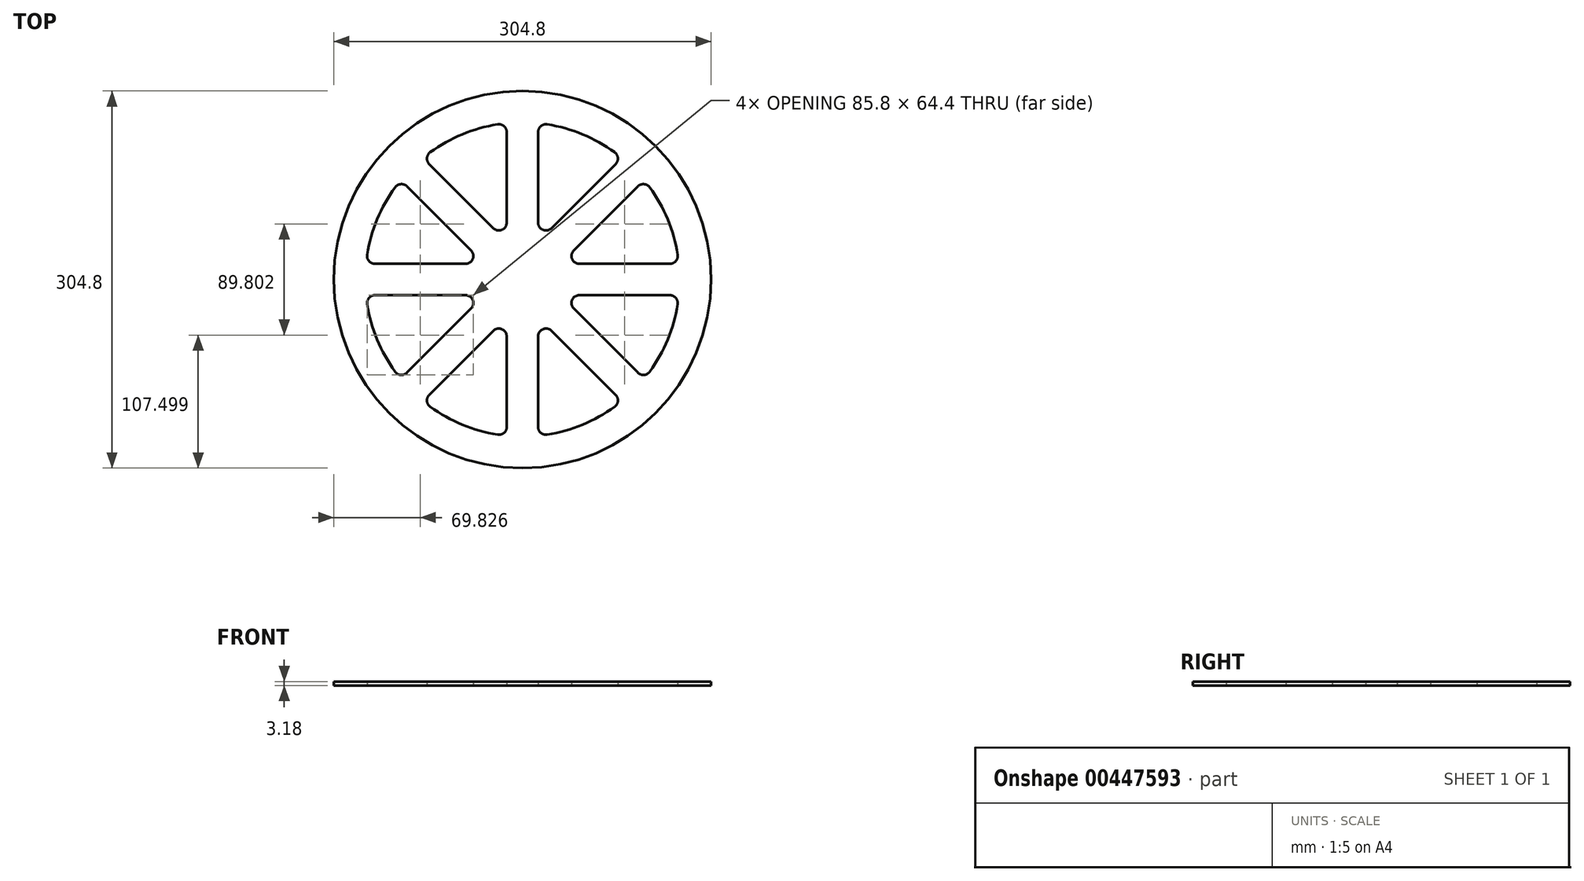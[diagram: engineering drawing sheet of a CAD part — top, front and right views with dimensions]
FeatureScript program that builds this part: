
annotation { "Feature Type Name" : "Feature", "Feature Type Description" : "" }
export const myFeature = defineFeature(function(context is Context, id is Id, definition is map)
    precondition{}
    {
        {
            var Q0;
            Q0=qCreatedBy(makeId("Top.planeOp"),FACE);
            var sketch = newSketch(context, id + "F0", { "sketchPlane" : qUnion([Q0])});
            skCircle(sketch, "E0", {"center": v(0, 0) * mm, "radius": 152.4 * mm});
            skArc(sketch, "E1", {"start": v(-125.4, -20.05) * mm, "mid": v(-117.33, -48.6) * mm, "end": v(-102.86, -74.5) * mm});
            skLineSegment(sketch, "E2.bottom", {"start": v(-119.14, 12.7) * mm, "end": v(-46, 12.7) * mm});
            skArc(sketch, "E3.trimOffspring", {"start": v(125.4, 20.05) * mm, "mid": v(117.33, 48.6) * mm, "end": v(102.86, 74.5) * mm});
            skPoint(sketch, "E4.visualSharp", {"position": v(-126.36, 12.7) * mm});
            skArc(sketch, "E4.filletArc", {"start": v(-125.4, 20.05) * mm, "mid": v(-123.97, 14.93) * mm, "end": v(-119.14, 12.7) * mm});
            skPoint(sketch, "E5.visualSharp", {"position": v(-126.36, -12.7) * mm});
            skArc(sketch, "E5.filletArc", {"start": v(-119.14, -12.7) * mm, "mid": v(-123.97, -14.93) * mm, "end": v(-125.4, -20.05) * mm});
            skPoint(sketch, "E6.visualSharp", {"position": v(126.36, -12.7) * mm});
            skArc(sketch, "E6.filletArc", {"start": v(125.4, -20.05) * mm, "mid": v(123.97, -14.93) * mm, "end": v(119.14, -12.7) * mm});
            skPoint(sketch, "E7.visualSharp", {"position": v(126.36, 12.7) * mm});
            skArc(sketch, "E7.filletArc", {"start": v(119.14, 12.7) * mm, "mid": v(123.97, 14.93) * mm, "end": v(125.4, 20.05) * mm});
            skPoint(sketch, "E8.1.0", {"position": v(80.37, 98.33) * mm});
            skPoint(sketch, "E8.1.1", {"position": v(-98.33, -80.37) * mm});
            skLineSegment(sketch, "E8.1.3", {"start": v(-93.22, -75.26) * mm, "end": v(-41.5, -23.54) * mm});
            skPoint(sketch, "E8.1.4", {"position": v(-80.37, -98.33) * mm});
            skPoint(sketch, "E8.1.5", {"position": v(98.33, 80.37) * mm});
            skLineSegment(sketch, "E8.1.6", {"start": v(-75.26, -93.22) * mm, "end": v(-23.54, -41.5) * mm});
            skArc(sketch, "E8.1.7", {"start": v(75.26, 93.22) * mm, "mid": v(77.1, 98.22) * mm, "end": v(74.5, 102.86) * mm});
            skArc(sketch, "E8.1.8", {"start": v(-75.26, -93.22) * mm, "mid": v(-77.1, -98.22) * mm, "end": v(-74.5, -102.86) * mm});
            skArc(sketch, "E8.1.9", {"start": v(-102.86, -74.5) * mm, "mid": v(-98.22, -77.1) * mm, "end": v(-93.22, -75.26) * mm});
            skArc(sketch, "E8.1.10", {"start": v(102.86, 74.5) * mm, "mid": v(98.22, 77.1) * mm, "end": v(93.22, 75.26) * mm});
            skPoint(sketch, "E8.2.0", {"position": v(-12.7, 126.36) * mm});
            skPoint(sketch, "E8.2.1", {"position": v(-12.7, -126.36) * mm});
            skLineSegment(sketch, "E8.2.3", {"start": v(-12.7, -119.14) * mm, "end": v(-12.7, -46) * mm});
            skPoint(sketch, "E8.2.4", {"position": v(12.7, -126.36) * mm});
            skPoint(sketch, "E8.2.5", {"position": v(12.7, 126.36) * mm});
            skLineSegment(sketch, "E8.2.6", {"start": v(12.7, -119.14) * mm, "end": v(12.7, -46) * mm});
            skArc(sketch, "E8.2.7", {"start": v(-12.7, 119.14) * mm, "mid": v(-14.93, 123.97) * mm, "end": v(-20.05, 125.4) * mm});
            skArc(sketch, "E8.2.8", {"start": v(12.7, -119.14) * mm, "mid": v(14.93, -123.97) * mm, "end": v(20.05, -125.4) * mm});
            skArc(sketch, "E8.2.9", {"start": v(-20.05, -125.4) * mm, "mid": v(-14.93, -123.97) * mm, "end": v(-12.7, -119.14) * mm});
            skArc(sketch, "E8.2.10", {"start": v(20.05, 125.4) * mm, "mid": v(14.93, 123.97) * mm, "end": v(12.7, 119.14) * mm});
            skPoint(sketch, "E8.3.0", {"position": v(-98.33, 80.37) * mm});
            skPoint(sketch, "E8.3.1", {"position": v(80.37, -98.33) * mm});
            skPoint(sketch, "E8.3.4", {"position": v(98.33, -80.37) * mm});
            skPoint(sketch, "E8.3.5", {"position": v(-80.37, 98.33) * mm});
            skLineSegment(sketch, "E8.3.6", {"start": v(93.22, -75.26) * mm, "end": v(41.5, -23.54) * mm});
            skArc(sketch, "E8.3.7", {"start": v(-93.22, 75.26) * mm, "mid": v(-98.22, 77.1) * mm, "end": v(-102.86, 74.5) * mm});
            skArc(sketch, "E8.3.8", {"start": v(93.22, -75.26) * mm, "mid": v(98.22, -77.1) * mm, "end": v(102.86, -74.5) * mm});
            skArc(sketch, "E8.3.9", {"start": v(74.5, -102.86) * mm, "mid": v(77.1, -98.22) * mm, "end": v(75.26, -93.22) * mm});
            skArc(sketch, "E8.3.10", {"start": v(-74.5, 102.86) * mm, "mid": v(-77.1, 98.22) * mm, "end": v(-75.26, 93.22) * mm});
            skLineSegment(sketch, "E8.4.3", {"start": v(119.14, -12.7) * mm, "end": v(46, -12.7) * mm});
            skPoint(sketch, "E8.5.0", {"position": v(-80.37, -98.33) * mm});
            skPoint(sketch, "E8.5.1", {"position": v(98.33, 80.37) * mm});
            skLineSegment(sketch, "E8.5.3", {"start": v(93.22, 75.26) * mm, "end": v(41.5, 23.54) * mm});
            skPoint(sketch, "E8.5.4", {"position": v(80.37, 98.33) * mm});
            skPoint(sketch, "E8.5.5", {"position": v(-98.33, -80.37) * mm});
            skArc(sketch, "E8.5.7", {"start": v(-75.26, -93.22) * mm, "mid": v(-77.1, -98.22) * mm, "end": v(-74.5, -102.86) * mm});
            skArc(sketch, "E8.5.8", {"start": v(75.26, 93.22) * mm, "mid": v(77.1, 98.22) * mm, "end": v(74.5, 102.86) * mm});
            skArc(sketch, "E8.5.9", {"start": v(102.86, 74.5) * mm, "mid": v(98.22, 77.1) * mm, "end": v(93.22, 75.26) * mm});
            skArc(sketch, "E8.5.10", {"start": v(-102.86, -74.5) * mm, "mid": v(-98.22, -77.1) * mm, "end": v(-93.22, -75.26) * mm});
            skPoint(sketch, "E8.6.0", {"position": v(12.7, -126.36) * mm});
            skPoint(sketch, "E8.6.1", {"position": v(12.7, 126.36) * mm});
            skLineSegment(sketch, "E8.6.3", {"start": v(12.7, 119.14) * mm, "end": v(12.7, 46) * mm});
            skPoint(sketch, "E8.6.4", {"position": v(-12.7, 126.36) * mm});
            skPoint(sketch, "E8.6.5", {"position": v(-12.7, -126.36) * mm});
            skLineSegment(sketch, "E8.6.6", {"start": v(-12.7, 119.14) * mm, "end": v(-12.7, 46) * mm});
            skArc(sketch, "E8.6.7", {"start": v(12.7, -119.14) * mm, "mid": v(14.93, -123.97) * mm, "end": v(20.05, -125.4) * mm});
            skArc(sketch, "E8.6.8", {"start": v(-12.7, 119.14) * mm, "mid": v(-14.93, 123.97) * mm, "end": v(-20.05, 125.4) * mm});
            skArc(sketch, "E8.6.9", {"start": v(20.05, 125.4) * mm, "mid": v(14.93, 123.97) * mm, "end": v(12.7, 119.14) * mm});
            skArc(sketch, "E8.6.10", {"start": v(-20.05, -125.4) * mm, "mid": v(-14.93, -123.97) * mm, "end": v(-12.7, -119.14) * mm});
            skPoint(sketch, "E8.7.0", {"position": v(98.33, -80.37) * mm});
            skPoint(sketch, "E8.7.1", {"position": v(-80.37, 98.33) * mm});
            skLineSegment(sketch, "E8.7.3", {"start": v(-75.26, 93.22) * mm, "end": v(-23.54, 41.5) * mm});
            skPoint(sketch, "E8.7.4", {"position": v(-98.33, 80.37) * mm});
            skPoint(sketch, "E8.7.5", {"position": v(80.37, -98.33) * mm});
            skLineSegment(sketch, "E8.7.6", {"start": v(-93.22, 75.26) * mm, "end": v(-41.5, 23.54) * mm});
            skArc(sketch, "E8.7.7", {"start": v(93.22, -75.26) * mm, "mid": v(98.22, -77.1) * mm, "end": v(102.86, -74.5) * mm});
            skArc(sketch, "E8.7.8", {"start": v(-93.22, 75.26) * mm, "mid": v(-98.22, 77.1) * mm, "end": v(-102.86, 74.5) * mm});
            skArc(sketch, "E8.7.9", {"start": v(-74.5, 102.86) * mm, "mid": v(-77.1, 98.22) * mm, "end": v(-75.26, 93.22) * mm});
            skArc(sketch, "E8.7.10", {"start": v(74.5, -102.86) * mm, "mid": v(77.1, -98.22) * mm, "end": v(75.26, -93.22) * mm});
            skArc(sketch, "E9.trimOffspring", {"start": v(-102.86, 74.5) * mm, "mid": v(-117.33, 48.6) * mm, "end": v(-125.4, 20.05) * mm});
            skArc(sketch, "E10.trimOffspring", {"start": v(74.5, 102.86) * mm, "mid": v(48.6, 117.33) * mm, "end": v(20.05, 125.4) * mm});
            skArc(sketch, "E11.trimOffspring", {"start": v(-20.05, 125.4) * mm, "mid": v(-48.6, 117.33) * mm, "end": v(-74.5, 102.86) * mm});
            skLineSegment(sketch, "E12.trimOffspring", {"start": v(-41.5, 23.54) * mm, "end": v(-93.22, 75.26) * mm});
            skLineSegment(sketch, "E13.trimOffspring", {"start": v(-46, 12.7) * mm, "end": v(-119.14, 12.7) * mm});
            skLineSegment(sketch, "E14.trimOffspring", {"start": v(-12.7, 46) * mm, "end": v(-12.7, 119.14) * mm});
            skLineSegment(sketch, "E15.trimOffspring", {"start": v(-23.54, 41.5) * mm, "end": v(-75.26, 93.22) * mm});
            skLineSegment(sketch, "E16.trimOffspring", {"start": v(46, 12.7) * mm, "end": v(119.14, 12.7) * mm});
            skLineSegment(sketch, "E17.trimOffspring", {"start": v(23.54, 41.5) * mm, "end": v(75.26, 93.22) * mm});
            skLineSegment(sketch, "E18.trimOffspring", {"start": v(12.7, 46) * mm, "end": v(12.7, 119.14) * mm});
            skLineSegment(sketch, "E19.trimOffspring", {"start": v(-12.7, -46) * mm, "end": v(-12.7, -119.14) * mm});
            skLineSegment(sketch, "E20.trimOffspring", {"start": v(-46, -12.7) * mm, "end": v(-119.14, -12.7) * mm});
            skLineSegment(sketch, "E21.trimOffspring", {"start": v(-41.5, -23.54) * mm, "end": v(-93.22, -75.26) * mm});
            skLineSegment(sketch, "E22.trimOffspring", {"start": v(-23.54, -41.5) * mm, "end": v(-75.26, -93.22) * mm});
            skLineSegment(sketch, "E23.trimOffspring", {"start": v(23.54, -41.5) * mm, "end": v(75.26, -93.22) * mm});
            skLineSegment(sketch, "E24.trimOffspring", {"start": v(12.7, -46) * mm, "end": v(12.7, -119.14) * mm});
            skLineSegment(sketch, "E25.trimOffspring", {"start": v(46, -12.7) * mm, "end": v(119.14, -12.7) * mm});
            skLineSegment(sketch, "E26.trimOffspring", {"start": v(41.5, -23.54) * mm, "end": v(93.22, -75.26) * mm});
            skLineSegment(sketch, "E27.trimOffspring", {"start": v(41.5, 23.54) * mm, "end": v(93.22, 75.26) * mm});
            skArc(sketch, "E28.trimOffspring", {"start": v(-74.5, -102.86) * mm, "mid": v(-48.6, -117.33) * mm, "end": v(-20.05, -125.4) * mm});
            skArc(sketch, "E29.trimOffspring", {"start": v(20.05, -125.4) * mm, "mid": v(48.6, -117.33) * mm, "end": v(74.5, -102.86) * mm});
            skArc(sketch, "E30.trimOffspring", {"start": v(102.86, -74.5) * mm, "mid": v(117.33, -48.6) * mm, "end": v(125.4, -20.05) * mm});
            skPoint(sketch, "E31.visualSharp", {"position": v(-12.7, 30.66) * mm});
            skArc(sketch, "E31.filletArc", {"start": v(-23.54, 41.5) * mm, "mid": v(-16.62, 40.12) * mm, "end": v(-12.7, 46) * mm});
            skPoint(sketch, "E32.visualSharp", {"position": v(-30.66, 12.7) * mm});
            skArc(sketch, "E32.filletArc", {"start": v(-46, 12.7) * mm, "mid": v(-40.12, 16.62) * mm, "end": v(-41.5, 23.54) * mm});
            skPoint(sketch, "E33.visualSharp", {"position": v(-30.66, -12.7) * mm});
            skArc(sketch, "E33.filletArc", {"start": v(-41.5, -23.54) * mm, "mid": v(-40.12, -16.62) * mm, "end": v(-46, -12.7) * mm});
            skPoint(sketch, "E34.visualSharp", {"position": v(-12.7, -30.66) * mm});
            skArc(sketch, "E34.filletArc", {"start": v(-12.7, -46) * mm, "mid": v(-16.62, -40.12) * mm, "end": v(-23.54, -41.5) * mm});
            skPoint(sketch, "E35.visualSharp", {"position": v(12.7, -30.66) * mm});
            skArc(sketch, "E35.filletArc", {"start": v(23.54, -41.5) * mm, "mid": v(16.62, -40.12) * mm, "end": v(12.7, -46) * mm});
            skPoint(sketch, "E36.visualSharp", {"position": v(30.66, -12.7) * mm});
            skArc(sketch, "E36.filletArc", {"start": v(46, -12.7) * mm, "mid": v(40.12, -16.62) * mm, "end": v(41.5, -23.54) * mm});
            skPoint(sketch, "E37.visualSharp", {"position": v(30.66, 12.7) * mm});
            skArc(sketch, "E37.filletArc", {"start": v(41.5, 23.54) * mm, "mid": v(40.12, 16.62) * mm, "end": v(46, 12.7) * mm});
            skPoint(sketch, "E38.visualSharp", {"position": v(12.7, 30.66) * mm});
            skArc(sketch, "E38.filletArc", {"start": v(12.7, 46) * mm, "mid": v(16.62, 40.12) * mm, "end": v(23.54, 41.5) * mm});
            skSolve(sketch);
        }
        {
            var Q0;
            Q0=makeQuery(id+"F0.imprint","IMPRINT",FACE,{"disambiguationData":[TD([[makeQuery(id+"F0.imprint","IMPRINT",EDGE,{"derivedFrom":sQuery(id+"F0.wireOp",EDGE,"E0")}),1.0]])]});
            extrude(context, id + "F1", {"entities" : qUnion([Q0]), "depth" : 3.17 * mm});
        }
    });
